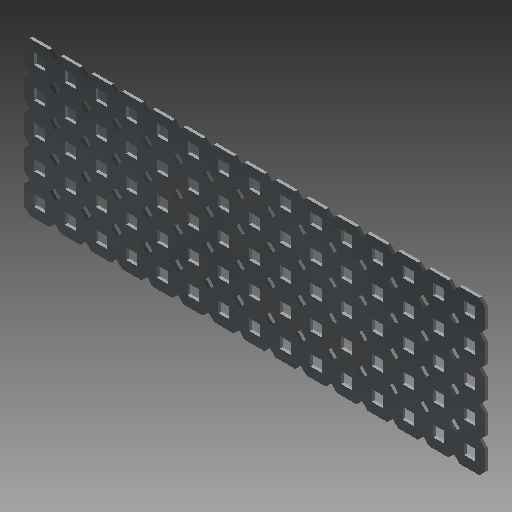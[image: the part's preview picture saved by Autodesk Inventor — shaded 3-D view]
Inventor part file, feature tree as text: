
AUTODESK INVENTOR PART (.ipt)
format: ipt  version: 2018 (Build 220112000, 112)  size: 837,632 bytes
history: native  units: mm (DEFAULTED — no unit token found)
features: other x76, extrude x75, pattern_linear x3, sketch x2, sheet_metal_op x1
ambient origin geometry x8: Origin, YZ Plane, XZ Plane, XY Plane, X Axis, Y Axis, Z Axis, Center Point
bodies: Solid1 (feature_tree)
feature tree (157):
  sheet_metal_op  "Face1"
  pattern_linear  "Rectangular Pattern1"  Spacing1=2.280986mm  [1 undecoded]
  pattern_linear  "Rectangular Pattern2"  Spacing1=2.280986mm  [1 undecoded]
  pattern_linear  "Rectangular Pattern3"  Spacing1=2.280986mm  [1 undecoded]
  sketch  "Sketch1"  dims[d0=12.7mm]
  other  "Plate1"
  sketch  "Sketch2"  dims[d1=12.7mm d2=2.280986mm d3=2.280986mm d4=2.280986mm d5=2.280986mm d6=2.280986mm d7=2.280986mm d8=2.280986mm d9=2.280986mm d10=4.572mm d11=4.572mm d12=4.064mm d13=4.064mm d14=1.17mm d15=150.0mm d17=12.7mm d18=50.0mm d20=12.7mm d21=25.4mm d22=0.0mm d23=150.0mm d25=12.7mm d26=50.0mm d28=12.7mm d29=0.0mm d30=0.0mm d31=0.0mm d32=0.0mm d33=0.0mm d34=0.0mm d35=0.0mm d36=0.0mm d37=0.0mm d38=0.0mm d39=0.0mm d40=0.0mm d41=0.0mm d42=0.0mm d43=0.0mm d44=0.0mm d45=0.0mm d46=0.0mm d47=0.0mm d48=0.0mm d49=0.0mm d50=0.0mm d51=0.0mm d52=0.0mm d53=0.0mm d54=0.0mm d55=0.0mm d56=0.0mm d57=0.0mm d58=0.0mm d59=0.0mm d60=0.0mm d61=0.0mm d62=0.0mm d63=0.0mm d64=0.0mm d65=0.0mm d66=0.0mm d67=0.0mm d68=0.0mm d69=0.0mm d70=0.0mm d71=0.0mm d72=0.0mm d73=0.0mm d74=0.0mm d75=0.0mm d76=0.0mm d77=0.0mm d78=0.0mm d79=0.0mm d80=0.0mm d81=0.0mm d82=0.0mm d83=0.0mm d84=0.0mm d85=0.0mm d86=0.0mm d87=0.0mm d88=0.0mm d89=0.0mm d90=0.0mm d91=0.0mm d92=0.0mm d93=0.0mm d94=0.0mm d95=0.0mm d96=0.0mm d97=0.0mm d98=0.0mm d99=0.0mm d100=0.0mm d101=0.0mm d102=0.0mm d103=0.0mm d104=0.0mm d105=0.0mm d106=0.0mm d107=0.0mm d108=0.0mm d109=0.0mm d110=0.0mm d111=0.0mm d112=0.0mm d113=0.0mm d114=0.0mm d115=0.0mm d116=0.0mm d117=0.0mm d118=0.0mm d119=0.0mm d120=0.0mm d121=0.0mm d122=0.0mm d123=0.0mm d124=0.0mm d125=0.0mm d126=0.0mm d127=0.0mm d128=0.0mm d129=0.0mm d130=0.0mm d131=0.0mm d132=0.0mm d133=0.0mm d134=0.0mm d135=0.0mm d136=0.0mm d137=0.0mm d138=0.0mm d139=0.0mm d140=0.0mm d141=0.0mm d142=0.0mm d143=0.0mm d144=0.0mm d145=0.0mm d146=0.0mm d147=0.0mm d148=0.0mm d149=0.0mm d150=0.0mm d151=0.0mm d152=0.0mm d153=0.0mm d154=0.0mm d155=0.0mm d156=0.0mm d157=0.0mm d158=0.0mm d159=0.0mm d160=0.0mm d161=0.0mm d162=0.0mm d163=0.0mm d164=0.0mm d165=0.0mm d166=0.0mm d167=0.0mm d168=0.0mm d169=0.0mm d170=0.0mm d171=0.0mm d172=0.0mm d173=0.0mm d174=0.0mm d175=0.0mm d176=0.0mm d177=0.0mm d178=0.0mm d179=1.17mm]
  other  "Srf1"
  other  "Srf2"
  other  "Srf3"
  other  "Srf4"
  other  "Srf5"
  other  "Srf6"
  other  "Srf7"
  other  "Srf8"
  other  "Srf9"
  other  "Srf10"
  other  "Srf11"
  other  "Srf12"
  other  "Srf13"
  other  "Srf14"
  other  "Srf15"
  other  "Srf16"
  other  "Srf17"
  other  "Srf18"
  other  "Srf19"
  other  "Srf20"
  other  "Srf21"
  other  "Srf22"
  other  "Srf23"
  other  "Srf24"
  other  "Srf25"
  other  "Srf26"
  other  "Srf27"
  other  "Srf28"
  other  "Srf29"
  other  "Srf30"
  other  "Srf31"
  other  "Srf32"
  other  "Srf33"
  other  "Srf34"
  other  "Srf35"
  other  "Srf36"
  other  "Srf37"
  other  "Srf38"
  other  "Srf39"
  other  "Srf40"
  other  "Srf41"
  other  "Srf42"
  other  "Srf43"
  other  "Srf44"
  other  "Srf45"
  other  "Srf46"
  other  "Srf47"
  other  "Srf48"
  other  "Srf49"
  other  "Srf50"
  other  "Srf51"
  other  "Srf52"
  other  "Srf53"
  other  "Srf54"
  other  "Srf55"
  other  "Srf56"
  other  "Srf57"
  other  "Srf58"
  other  "Srf59"
  other  "Srf60"
  other  "Srf61"
  other  "Srf62"
  other  "Srf63"
  other  "Srf64"
  other  "Srf65"
  other  "Srf66"
  other  "Srf67"
  other  "Srf68"
  other  "Srf69"
  other  "Srf70"
  other  "Srf71"
  other  "Srf72"
  other  "Srf73"
  other  "Srf74"
  other  "Srf75"
  extrude  "ExtrusionSrf1"  Depth=1.17mm
  extrude  "ExtrusionSrf2"  Depth=1.17mm
  extrude  "ExtrusionSrf3"  Depth=1.17mm
  extrude  "ExtrusionSrf4"  Depth=1.17mm
  extrude  "ExtrusionSrf5"  Depth=1.17mm
  extrude  "ExtrusionSrf6"  Depth=4.572mm
  extrude  "ExtrusionSrf7"  Depth=4.572mm
  extrude  "ExtrusionSrf8"  Depth=4.064mm
  extrude  "ExtrusionSrf9"  Depth=4.064mm
  extrude  "ExtrusionSrf10"  Depth=1.17mm
  extrude  "ExtrusionSrf11"  Depth=12.7mm
  extrude  "ExtrusionSrf12"  Depth=12.7mm
  extrude  "ExtrusionSrf13"  Depth=25.4mm TaperAngle=0.0deg
  extrude  "ExtrusionSrf14"  Depth=12.7mm
  extrude  "ExtrusionSrf15"  Depth=12.7mm
  extrude  "ExtrusionSrf16"  TaperAngle=0.0deg  [1 undecoded]
  extrude  "ExtrusionSrf17"  TaperAngle=0.0deg  [1 undecoded]
  extrude  "ExtrusionSrf18"  TaperAngle=0.0deg  [1 undecoded]
  extrude  "ExtrusionSrf19"  TaperAngle=0.0deg  [1 undecoded]
  extrude  "ExtrusionSrf20"  TaperAngle=0.0deg  [1 undecoded]
  extrude  "ExtrusionSrf21"  TaperAngle=0.0deg  [1 undecoded]
  extrude  "ExtrusionSrf22"  TaperAngle=0.0deg  [1 undecoded]
  extrude  "ExtrusionSrf23"  TaperAngle=0.0deg  [1 undecoded]
  extrude  "ExtrusionSrf24"  TaperAngle=0.0deg  [1 undecoded]
  extrude  "ExtrusionSrf25"  TaperAngle=0.0deg  [1 undecoded]
  extrude  "ExtrusionSrf26"  TaperAngle=0.0deg  [1 undecoded]
  extrude  "ExtrusionSrf27"  TaperAngle=0.0deg  [1 undecoded]
  extrude  "ExtrusionSrf28"  TaperAngle=0.0deg  [1 undecoded]
  extrude  "ExtrusionSrf29"  TaperAngle=0.0deg  [1 undecoded]
  extrude  "ExtrusionSrf30"  TaperAngle=0.0deg  [1 undecoded]
  extrude  "ExtrusionSrf31"  TaperAngle=0.0deg  [1 undecoded]
  extrude  "ExtrusionSrf32"  TaperAngle=0.0deg  [1 undecoded]
  extrude  "ExtrusionSrf33"  TaperAngle=0.0deg  [1 undecoded]
  extrude  "ExtrusionSrf34"  TaperAngle=0.0deg  [1 undecoded]
  extrude  "ExtrusionSrf35"  TaperAngle=0.0deg  [1 undecoded]
  extrude  "ExtrusionSrf36"  TaperAngle=0.0deg  [1 undecoded]
  extrude  "ExtrusionSrf37"  TaperAngle=0.0deg  [1 undecoded]
  extrude  "ExtrusionSrf38"  TaperAngle=0.0deg  [1 undecoded]
  extrude  "ExtrusionSrf39"  TaperAngle=0.0deg  [1 undecoded]
  extrude  "ExtrusionSrf40"  TaperAngle=0.0deg  [1 undecoded]
  extrude  "ExtrusionSrf41"  TaperAngle=0.0deg  [1 undecoded]
  extrude  "ExtrusionSrf42"  TaperAngle=0.0deg  [1 undecoded]
  extrude  "ExtrusionSrf43"  TaperAngle=0.0deg  [1 undecoded]
  extrude  "ExtrusionSrf44"  TaperAngle=0.0deg  [1 undecoded]
  extrude  "ExtrusionSrf45"  TaperAngle=0.0deg  [1 undecoded]
  extrude  "ExtrusionSrf46"  TaperAngle=0.0deg  [1 undecoded]
  extrude  "ExtrusionSrf47"  TaperAngle=0.0deg  [1 undecoded]
  extrude  "ExtrusionSrf48"  TaperAngle=0.0deg  [1 undecoded]
  extrude  "ExtrusionSrf49"  TaperAngle=0.0deg  [1 undecoded]
  extrude  "ExtrusionSrf50"  TaperAngle=0.0deg  [1 undecoded]
  extrude  "ExtrusionSrf51"  TaperAngle=0.0deg  [1 undecoded]
  extrude  "ExtrusionSrf52"  TaperAngle=0.0deg  [1 undecoded]
  extrude  "ExtrusionSrf53"  TaperAngle=0.0deg  [1 undecoded]
  extrude  "ExtrusionSrf54"  TaperAngle=0.0deg  [1 undecoded]
  extrude  "ExtrusionSrf55"  TaperAngle=0.0deg  [1 undecoded]
  extrude  "ExtrusionSrf56"  TaperAngle=0.0deg  [1 undecoded]
  extrude  "ExtrusionSrf57"  TaperAngle=0.0deg  [1 undecoded]
  extrude  "ExtrusionSrf58"  TaperAngle=0.0deg  [1 undecoded]
  extrude  "ExtrusionSrf59"  TaperAngle=0.0deg  [1 undecoded]
  extrude  "ExtrusionSrf60"  TaperAngle=0.0deg  [1 undecoded]
  extrude  "ExtrusionSrf61"  TaperAngle=0.0deg  [1 undecoded]
  extrude  "ExtrusionSrf62"  TaperAngle=0.0deg  [1 undecoded]
  extrude  "ExtrusionSrf63"  TaperAngle=0.0deg  [1 undecoded]
  extrude  "ExtrusionSrf64"  TaperAngle=0.0deg  [1 undecoded]
  extrude  "ExtrusionSrf65"  TaperAngle=0.0deg  [1 undecoded]
  extrude  "ExtrusionSrf66"  TaperAngle=0.0deg  [1 undecoded]
  extrude  "ExtrusionSrf67"  TaperAngle=0.0deg  [1 undecoded]
  extrude  "ExtrusionSrf68"  TaperAngle=0.0deg  [1 undecoded]
  extrude  "ExtrusionSrf69"  TaperAngle=0.0deg  [1 undecoded]
  extrude  "ExtrusionSrf70"  TaperAngle=0.0deg  [1 undecoded]
  extrude  "ExtrusionSrf71"  TaperAngle=0.0deg  [1 undecoded]
  extrude  "ExtrusionSrf72"  TaperAngle=0.0deg  [1 undecoded]
  extrude  "ExtrusionSrf73"  TaperAngle=0.0deg  [1 undecoded]
  extrude  "ExtrusionSrf74"  TaperAngle=0.0deg  [1 undecoded]
  extrude  "ExtrusionSrf75"  TaperAngle=0.0deg  [1 undecoded]
note: 63 required parameter values undecoded (feature->parameter linkage not recoverable at this tier; creation-order binding heuristic only, values carry confidence <= 0.55)
